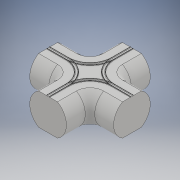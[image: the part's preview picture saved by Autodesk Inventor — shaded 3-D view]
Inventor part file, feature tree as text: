
AUTODESK INVENTOR PART (.ipt)
format: ipt  version: 2017 (Build 210142000, 142)  size: 449,536 bytes
history: native  units: in
note: dims shown in document units (in); Inventor stores cm internally (conversion verified against a paired STEP export)
features: sketch x6, extrude x3, mirror x3, plane x1, sweep x1, other x1
ambient origin geometry x8: Origin, YZ Plane, XZ Plane, XY Plane, X Axis, Y Axis, Z Axis, Center Point
bodies: Body1 (feature_tree)
feature tree (15):
  sketch  "Sketch1"  dims[d0=6.6667in d2=9.7746in d5=-4.8873in d62=45.0deg d71=4.0in d72=0.0in]
  extrude  "corridor eighth"  Depth=4.0in TaperAngle=45.0deg
  plane  "Work Plane1"
  sketch  "Sketch17"  dims[d170=10.3167in d171=10.3167in]
  sketch  "Sketch7"  dims[d160=4.0in d168=10.3167in d169=10.3167in]
  sweep  "curve"
  mirror  "mirror plane YZ"
  extrude  "corridor eighth complete"  Depth=10.3167in
  mirror  "Mirror half"
  mirror  "Mirrorfull"
  extrude  "hole fill in"  Depth=0.0625in
  other  "corridor"
  sketch  "Sketch22"  dims[d196=4.0in d197=0.5833in d198=3.8873in d199=3.8873in d200=1.7083in d201=0.0625in d202=0.0625in d203=1.6458in d204=0.25in d205=0.125in d207=0.0884in d208=45.0deg d209=3.3333in d210=0.125in d211=1.0in]
  sketch  "Sketch23"  dims[d212=0.0in d213=0.0in]
  sketch  "Sketch24"  dims[d214=4.0in d215=0.0in d216=4.0in d217=0.0in]
